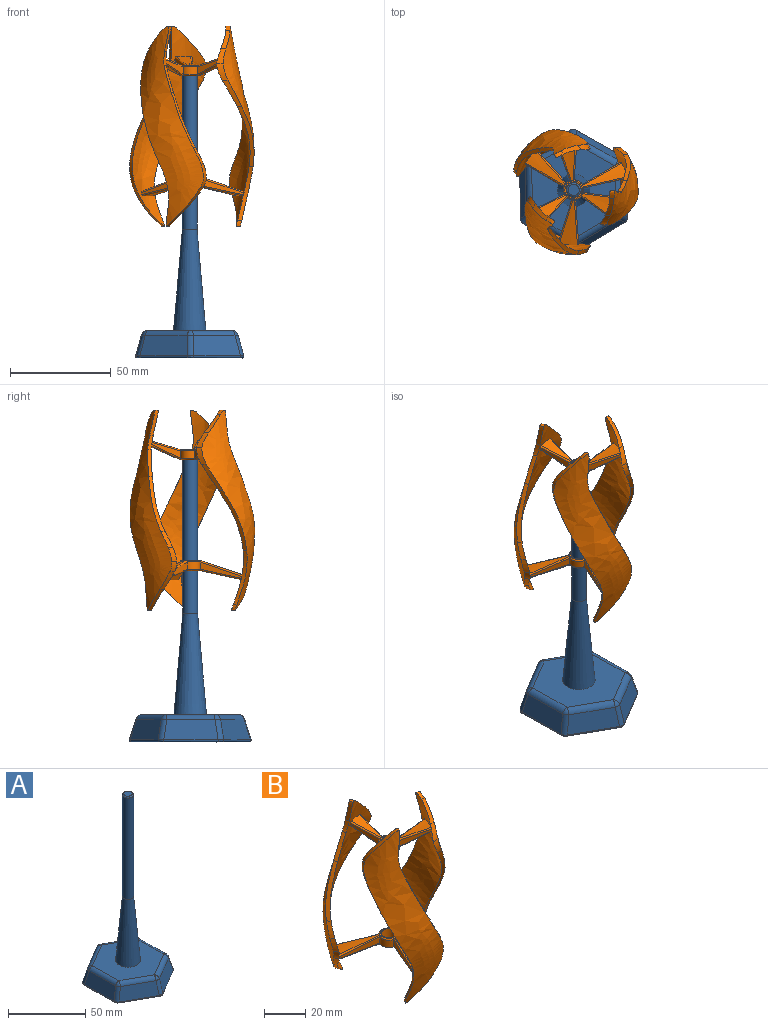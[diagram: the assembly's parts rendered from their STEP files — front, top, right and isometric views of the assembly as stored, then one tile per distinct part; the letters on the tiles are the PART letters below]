
ASSEMBLY  parts=2 mates=1
PART A: 42 faces, bbox 53.7x60.8x145 mm
  f0: torus R=2.78mm, axis (0,0,1), area 28.7mm2, adj f1,f2
  f1: cylinder r=3.65mm len=80.16mm, axis (0,0,-1), area 1838.3mm2, adj f0,f3
  f2: plane 5.56x5.56mm, normal (0,0,1), area 24.2mm2, adj f0
  f3: cone r=8.05mm half-angle=5deg, axis (0,0,-1), area 1858.5mm2, adj f1,f39
  f4: cylinder r=0.84mm len=23.94mm, axis (0.87,-0.49,0), area 41.5mm2, adj f5,f15,f21,f22
  f5: bspline ~3.3x1.37mm, area 4.9mm2, adj f4,f6,f22,f36
  f6: cylinder r=0.84mm len=23.57mm, axis (0.86,0.51,0), area 41.5mm2, adj f5,f7,f22,f38
  f7: bspline ~2.88x2.06mm, area 4.9mm2, adj f6,f8,f22,f34
  f8: cylinder r=0.84mm len=26.96mm, axis (-0.01,1,0), area 41.5mm2, adj f7,f9,f22,f40
  f9: bspline ~2.85x2.12mm, area 4.9mm2, adj f8,f10,f22,f32
  f10: cylinder r=0.84mm len=23.94mm, axis (-0.87,0.49,0), area 41.5mm2, adj f9,f11,f22,f41
  f11: bspline ~3.3x1.37mm, area 4.9mm2, adj f10,f12,f16,f22
  f12: cylinder r=0.84mm len=23.57mm, axis (-0.86,-0.51,0), area 41.5mm2, adj f11,f13,f17,f22
  f13: bspline ~2.88x2.06mm, area 4.9mm2, adj f12,f14,f18,f22
  f14: cylinder r=0.84mm len=26.96mm, axis (0.01,-1,0), area 41.5mm2, adj f13,f15,f19,f22
  f15: bspline ~2.85x2.12mm, area 4.9mm2, adj f4,f14,f20,f22
  f16: cylinder r=3.36mm len=10.2mm, axis (0,0.3,0.96), area 35.7mm2, adj f11,f17,f26,f41
  f17: plane 23.19x15.33mm, normal (0.49,-0.83,0.26), area 265mm2, adj f12,f16,f18,f27
  f18: cylinder r=3.36mm len=10.2mm, axis (-0.26,0.14,0.96), area 35.7mm2, adj f13,f17,f19,f24
  f19: plane 26.95x10.08mm, normal (0.97,0.01,0.26), area 265mm2, adj f14,f18,f20,f37
  f20: cylinder r=3.36mm len=10.2mm, axis (-0.25,-0.15,0.96), area 35.7mm2, adj f15,f19,f21,f23
  f21: plane 23.53x14.74mm, normal (0.47,0.84,0.26), area 265mm2, adj f4,f20,f35,f36
  f22: plane 59.03x51.99mm, normal (0,0,-1), area 2298.8mm2, adj f4,f5,f6,f7,f8,f9,f10,f11
  f23: sphere r=3.36mm, area 7mm2, adj f20,f35,f37
  f24: sphere r=3.36mm, area 7mm2, adj f18,f27,f37
  f25: sphere r=3.36mm, area 9.3mm2, adj f33,f35,f36
  f26: sphere r=3.36mm, area 11.5mm2, adj f16,f27,f30
  f27: cylinder r=3.36mm len=22.13mm, axis (0.86,0.51,0), area 104.8mm2, adj f17,f24,f26,f39
  f28: sphere r=3.36mm, area 6.8mm2, adj f31,f33,f34
  f29: sphere r=3.36mm, area 8.2mm2, adj f30,f31,f32
  f30: cylinder r=3.36mm len=22.39mm, axis (0.87,-0.49,0), area 104.8mm2, adj f26,f29,f39,f41
  f31: cylinder r=3.36mm len=23.88mm, axis (0.01,-1,0), area 104.8mm2, adj f28,f29,f39,f40
  f32: cylinder r=3.36mm len=10.2mm, axis (0.25,0.15,0.96), area 35.7mm2, adj f9,f29,f40,f41
  f33: cylinder r=3.36mm len=22.13mm, axis (-0.86,-0.51,0), area 104.8mm2, adj f25,f28,f38,f39
  f34: cylinder r=3.36mm len=10.2mm, axis (0.26,-0.14,0.96), area 35.7mm2, adj f7,f28,f38,f40
  f35: cylinder r=3.36mm len=22.39mm, axis (-0.87,0.49,0), area 104.8mm2, adj f21,f23,f25,f39
  f36: cylinder r=3.36mm len=10.2mm, axis (0,-0.3,0.96), area 35.7mm2, adj f5,f21,f25,f38
  f37: cylinder r=3.36mm len=23.88mm, axis (-0.01,1,0), area 104.8mm2, adj f19,f23,f24,f39
  f38: plane 23.19x15.33mm, normal (-0.49,0.83,0.26), area 265mm2, adj f6,f33,f34,f36
  f39: plane 47.66x41.62mm, normal (0,0,1), area 1271.8mm2, adj f3,f27,f30,f31,f33,f35,f37
  f40: plane 26.95x10.08mm, normal (-0.97,-0.01,0.26), area 265mm2, adj f8,f31,f32,f34
  f41: plane 23.53x14.74mm, normal (-0.47,-0.84,0.26), area 265mm2, adj f10,f16,f30,f32
PART B: 124 faces, bbox 101.1x115x101.7 mm
  f0: bspline ~55.27x6.89mm, area 19.3mm2, adj f1,f9,f17,f18
  f1: bspline ~55.27x8.04mm, area 21.9mm2, adj f0,f2,f17,f18
  f2: bspline ~55.27x26.98mm, area 66.3mm2, adj f1,f3,f17,f18
  f3: bspline ~55.27x13.78mm, area 30.8mm2, adj f2,f4,f17,f18
  f4: bspline ~55.27x6.89mm, area 14.2mm2, adj f3,f5,f17,f18
  f5: bspline ~55.27x12.06mm, area 24.7mm2, adj f4,f6,f17,f18
  f6: bspline ~55.27x4.02mm, area 10.1mm2, adj f5,f7,f17,f18
  f7: bspline ~55.27x9.19mm, area 29.4mm2, adj f6,f8,f17,f18
  f8: bspline ~55.27x7.46mm, area 24mm2, adj f7,f16,f17,f18
  f9: bspline ~55.27x5.17mm, area 15.4mm2, adj f0,f10,f17,f18
  f10: bspline ~55.27x8.61mm, area 27.2mm2, adj f9,f11,f17,f18
  f11: bspline ~55.27x11.19mm, area 33.3mm2, adj f10,f12,f17,f18
  f12: bspline ~55.27x3.4mm, area 6.8mm2, adj f11,f13,f17,f18
  f13: bspline ~55.27x26.41mm, area 56.1mm2, adj f12,f14,f17,f18
  f14: bspline ~55.27x29.85mm, area 68.8mm2, adj f13,f15,f17,f18
  f15: bspline ~55.27x13.2mm, area 35.9mm2, adj f14,f16,f17,f18
  f16: bspline ~55.27x8.04mm, area 24mm2, adj f8,f15,f17,f18
  f17: bspline ~100.67x60.47mm, area 1637mm2, adj f0,f1,f2,f3,f4,f5,f6,f7
  f18: bspline ~100x65.48mm, area 1635.9mm2, adj f0,f1,f2,f3,f4,f5,f6,f7
  f19: bspline ~6.89x4.31mm, area 19.3mm2, adj f20,f28,f36,f37
  f20: bspline ~49.3x30.12mm, area 21.9mm2, adj f19,f21,f36,f37
  f21: bspline ~26.98x12.87mm, area 66.3mm2, adj f20,f22,f36,f37
  f22: bspline ~50.74x32.61mm, area 30.8mm2, adj f21,f23,f36,f37
  f23: bspline ~6.89x3.33mm, area 14.2mm2, adj f22,f24,f36,f37
  f24: bspline ~12.06x4.3mm, area 24.7mm2, adj f23,f25,f36,f37
  f25: bspline ~49.87x31.12mm, area 10.1mm2, adj f24,f26,f36,f37
  f26: bspline ~9.71x9.19mm, area 29.4mm2, adj f25,f27,f36,f37
  f27: bspline ~7.46x5.91mm, area 24mm2, adj f26,f35,f36,f37
  f28: bspline ~48.73x29.13mm, area 15.4mm2, adj f19,f29,f36,f37
  f29: bspline ~8.61x7.81mm, area 27.2mm2, adj f28,f30,f36,f37
  f30: bspline ~53.46x37.33mm, area 33.3mm2, adj f29,f31,f36,f37
  f31: bspline ~2.93x2.7mm, area 6.8mm2, adj f30,f32,f36,f37
  f32: bspline ~50.5x32.19mm, area 56.1mm2, adj f31,f33,f36,f37
  f33: bspline ~29.85x16.33mm, area 68.8mm2, adj f32,f34,f36,f37
  f34: bspline ~50.16x31.61mm, area 35.9mm2, adj f33,f35,f36,f37
  f35: bspline ~48.2x28.22mm, area 24mm2, adj f27,f34,f36,f37
  f36: bspline ~100.67x67.48mm, area 1635.6mm2, adj f19,f20,f21,f22,f23,f24,f25,f26
  f37: bspline ~100x73.07mm, area 1635.9mm2, adj f19,f20,f21,f22,f23,f24,f25,f26
  f38: bspline ~6.89x4.31mm, area 19.3mm2, adj f39,f47,f55,f56
  f39: bspline ~49.3x30.12mm, area 21.9mm2, adj f38,f40,f55,f56
  f40: bspline ~26.98x12.87mm, area 66.3mm2, adj f39,f41,f55,f56
  f41: bspline ~50.74x32.61mm, area 30.8mm2, adj f40,f42,f55,f56
  f42: bspline ~6.89x3.33mm, area 14.2mm2, adj f41,f43,f55,f56
  f43: bspline ~48.68x29.04mm, area 24.7mm2, adj f42,f44,f55,f56
  f44: bspline ~4.59x3.93mm, area 10.1mm2, adj f43,f45,f55,f56
  f45: bspline ~52.17x35.09mm, area 29.4mm2, adj f44,f46,f55,f56
  f46: bspline ~7.46x5.91mm, area 24mm2, adj f45,f54,f55,f56
  f47: bspline ~48.73x29.13mm, area 15.4mm2, adj f38,f48,f55,f56
  f48: bspline ~8.61x7.81mm, area 27.2mm2, adj f47,f49,f55,f56
  f49: bspline ~53.46x37.33mm, area 33.3mm2, adj f48,f50,f55,f56
  f50: bspline ~48.26x28.32mm, area 6.8mm2, adj f49,f51,f55,f56
  f51: bspline ~26.41x8.07mm, area 56.1mm2, adj f50,f52,f55,f56
  f52: bspline ~54.9x39.82mm, area 68.8mm2, adj f51,f53,f55,f56
  f53: bspline ~50.16x31.61mm, area 35.9mm2, adj f52,f54,f55,f56
  f54: bspline ~48.2x28.22mm, area 24mm2, adj f46,f53,f55,f56
  f55: bspline ~100.67x67.48mm, area 1635mm2, adj f38,f39,f40,f41,f42,f43,f44,f45
  f56: bspline ~100x73.07mm, area 1635.9mm2, adj f38,f39,f40,f41,f42,f43,f44,f45
  f57: torus R=4.35mm, axis (0,0,-1), area 7.7mm2, adj f58,f59,f61,f70
  f58: cylinder r=5mm len=6.26mm, axis (0,0,1), area 28.6mm2, adj f57,f59,f61,f62,f76,f78,f83,f88
  f59: bspline ~16.61x8.06mm, area 18.6mm2, adj f36,f57,f58,f60,f70,f88
  f60: cone r=5mm half-angle=66.3deg, axis (0,0,1), area 69.4mm2, adj f36,f59,f67,f70
  f61: bspline ~17.07x8.73mm, area 18.4mm2, adj f55,f57,f58,f62,f70,f90
  f62: plane 14.82x8.13mm, normal (-0.41,0.91,0), area 37.9mm2, adj f55,f58,f61,f78
  f63: torus R=4.35mm, axis (0,0,-1), area 8.3mm2, adj f64,f65,f67,f70
  f64: cylinder r=5mm len=5.73mm, axis (0,0,1), area 30.5mm2, adj f63,f65,f67,f68,f80,f81,f82,f83
  f65: bspline ~16.98x8.06mm, area 18.6mm2, adj f17,f63,f64,f66,f70,f82
  f66: cone r=5mm half-angle=66.3deg, axis (0,0,1), area 71.3mm2, adj f17,f65,f70,f73
  f67: bspline ~17.32x8.06mm, area 18.6mm2, adj f36,f60,f63,f64,f68,f70
  f68: plane 16.21x8.1mm, normal (1,-0.06,0), area 37.7mm2, adj f36,f64,f67,f80
  f69: torus R=4.35mm, axis (0,0,-1), area 9mm2, adj f70,f71,f73,f89
  f70: plane 9.54x9.4mm, normal (0,0,-1), area 17.9mm2, adj f57,f59,f60,f61,f63,f65,f66,f67
  f71: bspline ~15.14x11.97mm, area 19mm2, adj f55,f69,f70,f72,f89,f90
  f72: plane 12.96x9.86mm, normal (0.8,-0.61,0), area 37.7mm2, adj f55,f71,f83,f86,f89
  f73: bspline ~16.05x10.74mm, area 18.6mm2, adj f17,f66,f69,f70,f74,f89
  f74: plane 13.54x8.99mm, normal (-0.55,-0.83,0), area 37.7mm2, adj f17,f73,f85,f89
  f75: cone r=22.75mm half-angle=74.3deg, axis (0,0,1), area 63.5mm2, adj f36,f76,f80,f83
  f76: bspline ~15.5x5.86mm, area 17mm2, adj f36,f58,f75,f83,f88
  f77: cone r=22.75mm half-angle=74.3deg, axis (0,0,1), area 82.7mm2, adj f55,f78,f83,f86
  f78: bspline ~15.21x7.23mm, area 17.1mm2, adj f55,f58,f62,f77,f83
  f79: cone r=22.75mm half-angle=74.3deg, axis (0,0,1), area 69.3mm2, adj f17,f81,f83,f85
  f80: bspline ~16.37x5.18mm, area 17mm2, adj f36,f64,f68,f75,f83
  f81: bspline ~16.3x5.18mm, area 17mm2, adj f17,f64,f79,f82,f83
  f82: plane 16.01x8.11mm, normal (0.17,0.99,0), area 37.7mm2, adj f17,f64,f65,f81
  f83: torus R=4.35mm, axis (0,0,-1), area 26.9mm2, adj f58,f64,f72,f75,f76,f77,f78,f79
  f84: plane 8.7x8.7mm, normal (0,0,1), area 15.3mm2, adj f83,f87
  f85: bspline ~15.34x10.63mm, area 16.9mm2, adj f17,f74,f79,f83,f89
  f86: bspline ~13.53x10.33mm, area 16.8mm2, adj f55,f72,f77,f83
  f87: cylinder r=3.75mm len=7.5mm, axis (0,0,-1), area 117.8mm2, adj f70,f84
  f88: plane 15.39x8.1mm, normal (-0.95,-0.32,0), area 37.7mm2, adj f36,f58,f59,f76
  f89: cylinder r=5mm len=7.74mm, axis (0,0,1), area 32.9mm2, adj f69,f71,f72,f73,f74,f83,f85
  f90: cone r=5mm half-angle=66.3deg, axis (0,0,1), area 90.1mm2, adj f55,f61,f70,f71
  f91: torus R=4.35mm, axis (0,0,-1), area 8.9mm2, adj f92,f93,f95,f97
  f92: plane 9.45x9.14mm, normal (0,0,1), area 17.9mm2, adj f91,f93,f94,f95,f113,f114,f115,f116
  f93: bspline ~24.13x8.68mm, area 24.5mm2, adj f17,f91,f92,f94,f97,f123
  f94: cone r=28.73mm half-angle=71.8deg, axis (0,0,-1), area 111.6mm2, adj f17,f92,f93,f114
  f95: bspline ~24.73x8.69mm, area 24.2mm2, adj f55,f91,f92,f96,f97,f118
  f96: plane 22.26x8.28mm, normal (1,0,0), area 51.6mm2, adj f55,f95,f97,f101
  f97: cylinder r=5mm len=6.37mm, axis (0,0,-1), area 32.7mm2, adj f91,f93,f95,f96,f101,f104,f123
  f98: cone r=4.65mm half-angle=78.2deg, axis (0,0,-1), area 98.2mm2, adj f17,f99,f104,f107
  f99: bspline ~23.88x5.71mm, area 22.9mm2, adj f17,f98,f104,f123
  f100: cone r=4.65mm half-angle=78.2deg, axis (0,0,-1), area 198.8mm2, adj f36,f55,f101,f102,f104,f109,f111,f122
  f101: bspline ~24.22x5.68mm, area 23mm2, adj f55,f96,f97,f100,f104
  f102: bspline ~22.96x7.54mm, area 22.8mm2, adj f55,f100,f103,f122
  f103: plane 21.3x8.27mm, normal (-0.96,0.29,0), area 51.5mm2, adj f55,f102,f117,f122
  f104: torus R=4.35mm, axis (0,0,-1), area 21.2mm2, adj f97,f98,f99,f100,f101,f105,f106,f107
  f105: cylinder r=5mm len=7.42mm, axis (0,0,-1), area 30.9mm2, adj f104,f107,f108,f110,f113,f114,f115
  f106: plane 8.7x8.7mm, normal (0,0,-1), area 15.3mm2, adj f104,f121
  f107: bspline ~19.54x11.71mm, area 23.2mm2, adj f17,f98,f104,f105,f108
  f108: plane 19.39x11.11mm, normal (-0.5,0.87,0), area 51.9mm2, adj f17,f105,f107,f114
  f109: bspline ~16.94x15.59mm, area 22.9mm2, adj f36,f100,f104,f110
  f110: plane 16.34x15.12mm, normal (0.73,0.68,0), area 51.4mm2, adj f36,f104,f105,f109,f115
  f111: bspline ~21.93x10.93mm, area 22.9mm2, adj f36,f100,f112,f122
  f112: plane 20.06x9.69mm, normal (-0.43,-0.9,0), area 51.6mm2, adj f36,f111,f119,f122
  f113: torus R=4.35mm, axis (0,0,-1), area 8.3mm2, adj f92,f105,f114,f115
  f114: bspline ~20.55x11.94mm, area 24.1mm2, adj f17,f92,f94,f105,f108,f113
  f115: bspline ~18.42x17.31mm, area 24.6mm2, adj f36,f92,f105,f110,f113,f120
  f116: torus R=4.35mm, axis (0,0,-1), area 7.9mm2, adj f92,f117,f119,f122
  f117: bspline ~22.44x8.19mm, area 24.3mm2, adj f55,f92,f103,f116,f118,f122
  f118: cone r=28.73mm half-angle=71.8deg, axis (0,0,-1), area 90.3mm2, adj f55,f92,f95,f117
  f119: bspline ~22.27x11.34mm, area 24.2mm2, adj f36,f92,f112,f116,f120,f122
  f120: cone r=28.73mm half-angle=71.8deg, axis (0,0,-1), area 114.6mm2, adj f36,f92,f115,f119
  f121: cylinder r=3.75mm len=7.5mm, axis (0,0,-1), area 117.8mm2, adj f92,f106
  f122: cylinder r=5mm len=7.11mm, axis (0,0,-1), area 34.5mm2, adj f100,f102,f103,f111,f112,f116,f117,f119
  f123: plane 21.75x8.25mm, normal (0.21,-0.98,0), area 51.4mm2, adj f17,f93,f97,f99,f104
PLACE A rot(axis=(0,0.09,1),0deg) t=(0.45,-1.75,-5.6)mm fixed
PLACE B rot(axis=(0,0,1),119.7deg) t=(0.45,-1.75,-4.57)mm
MATE revolute A.f3 <-> B.f98  axis (0,0,1) through (0.45,-1.75,75.43)mm
